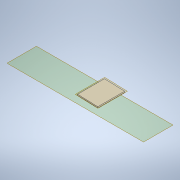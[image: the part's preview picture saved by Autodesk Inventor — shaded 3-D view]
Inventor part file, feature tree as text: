
AUTODESK INVENTOR PART (.ipt)
format: ipt  version: 2020.2 (Build 242310000, 310)  size: 125,952 bytes
history: native  units: mm
features: extrude x3, sketch x3, other x2
ambient origin geometry x8: Origin, YZ Plane, XZ Plane, XY Plane, X Axis, Y Axis, Z Axis, Center Point
bodies: Solide1 (feature_tree)
feature tree (8):
  extrude  "Extrusion1"  Depth=785.7mm
  other  "Plan de construction1"
  extrude  "Extrusion2"  Depth=3.0mm
  other  "Plan de construction2"
  extrude  "Extrusion3"  Depth=65.0mm TaperAngle=0.0deg
  sketch  "Esquisse1"
  sketch  "Esquisse2"
  sketch  "Esquisse3"
